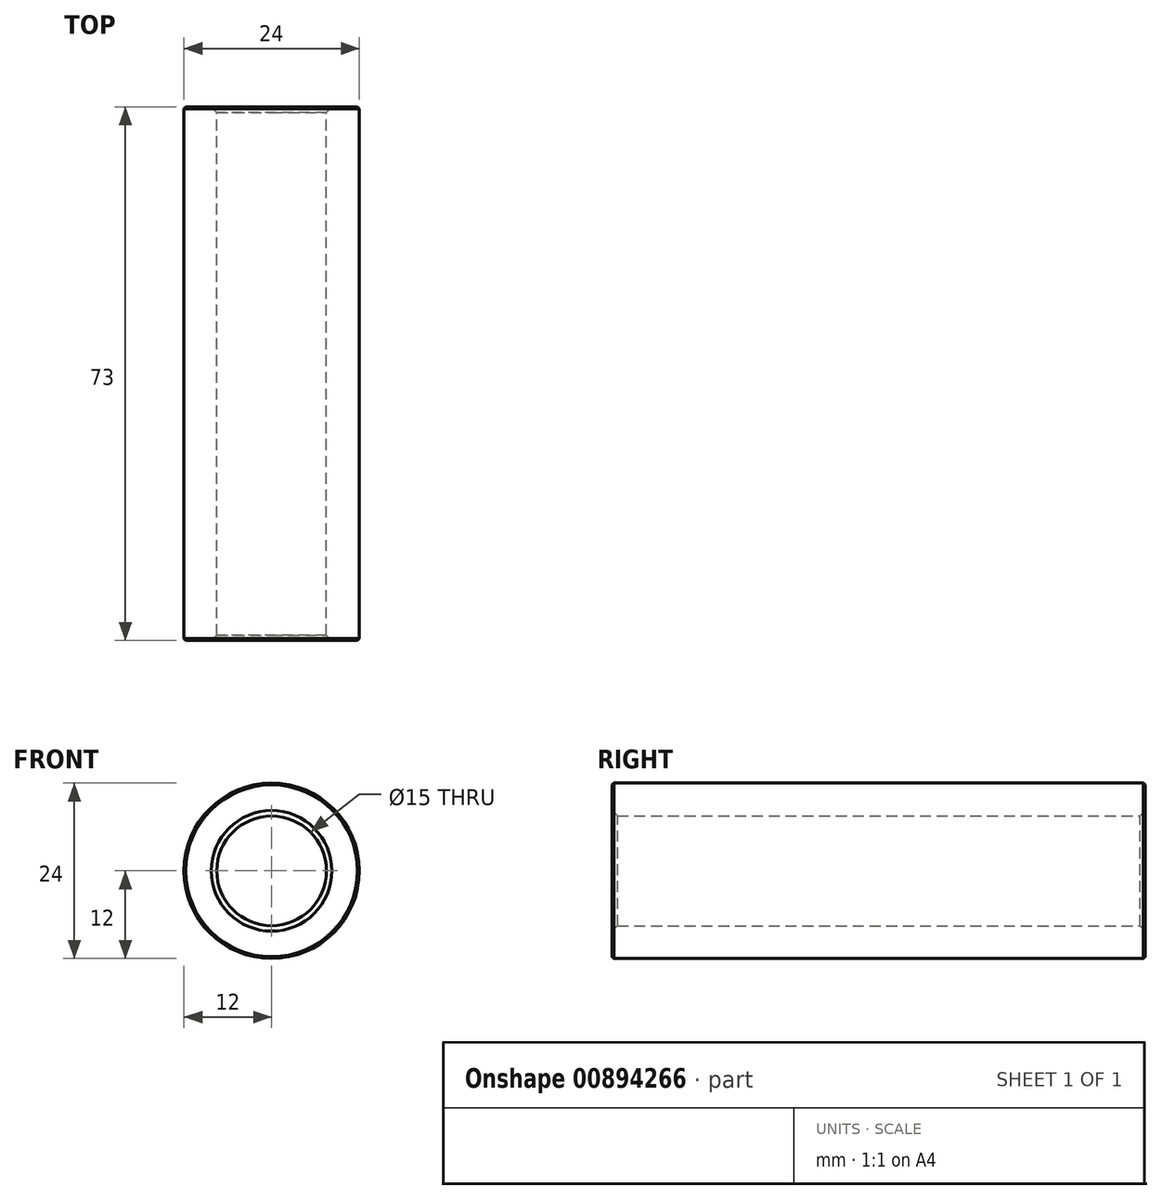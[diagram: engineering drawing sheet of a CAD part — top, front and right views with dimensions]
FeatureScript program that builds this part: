
annotation { "Feature Type Name" : "Feature", "Feature Type Description" : "" }
export const myFeature = defineFeature(function(context is Context, id is Id, definition is map)
    precondition{}
    {
        {
            var Q0;
            Q0=qCreatedBy(makeId("Front.planeOp"),FACE);
            var sketch = newSketch(context, id + "F0", { "sketchPlane" : qUnion([Q0])});
            skCircle(sketch, "E0", {"center": v(0, 0) * mm, "radius": 7.5 * mm});
            skCircle(sketch, "E1", {"center": v(0, 0) * mm, "radius": 12 * mm});
            skSolve(sketch);
        }
        {
            var Q0;
            Q0=makeQuery(id+"F0.imprint","IMPRINT",FACE,{"disambiguationData":[TD([[makeQuery(id+"F0.imprint","IMPRINT",EDGE,{"derivedFrom":sQuery(id+"F0.wireOp",EDGE,"E0")}),-1.0]])]});
            extrude(context, id + "F1", {"entities" : qUnion([Q0]), "depth" : 73 * mm, "offsetDistance" : 25 * mm});
        }
        {
            var Q0;
            Q0=makeQuery(id+"F1.opExtrude","CAP_EDGE",EDGE,{"disambiguationData":[OSD([sQuery(id+"F0.wireOp",EDGE,"E1")])],"isStart":false});
            var Q1;
            Q1=makeQuery(id+"F1.opExtrude","CAP_EDGE",EDGE,{"disambiguationData":[OSD([sQuery(id+"F0.wireOp",EDGE,"E1")])],"isStart":true});
            chamfer(context, id + "F2", {"entities" : qUnion([Q0, Q1]), "width" : 0.25 * mm, "tangentPropagation" : true});
        }
        {
            var Q0;
            Q0=makeQuery(id+"F1.opExtrude","CAP_EDGE",EDGE,{"disambiguationData":[OSD([sQuery(id+"F0.wireOp",EDGE,"E0")])],"isStart":false});
            var Q1;
            Q1=makeQuery(id+"F1.opExtrude","CAP_EDGE",EDGE,{"disambiguationData":[OSD([sQuery(id+"F0.wireOp",EDGE,"E0")])],"isStart":true});
            chamfer(context, id + "F3", {"entities" : qUnion([Q0, Q1]), "width" : 0.75 * mm, "tangentPropagation" : true});
        }
    });
